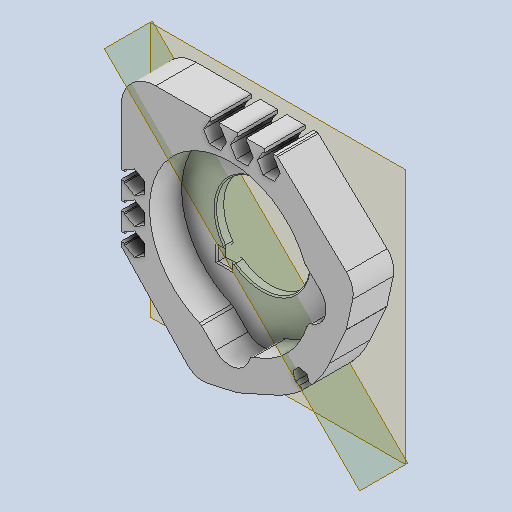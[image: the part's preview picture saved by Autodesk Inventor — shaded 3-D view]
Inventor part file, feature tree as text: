
AUTODESK INVENTOR PART (.ipt)
format: ipt  version: 2022 (Build 260153000, 153)  size: 334,848 bytes
history: native  units: in
note: dims shown in document units (in); Inventor stores cm internally (conversion verified against a paired STEP export)
features: other x3, sketch x3, plane x2
ambient origin geometry x8: Origin, YZ Plane, XZ Plane, XY Plane, X Axis, Y Axis, Z Axis, Center Point
bodies: Solid1 (feature_tree)
feature tree (8):
  other  "uppermidblock_MIR.ipt"
  other  "Solid1::uppermidblock_MIR.ipt"
  other  "TaggingFeature1"
  sketch  "Sketch1"  dims[d0=0.3937in]
  sketch  "Sketch2"
  sketch  "Sketch3"
  plane  "Work Plane1"
  plane  "Work Plane2"
